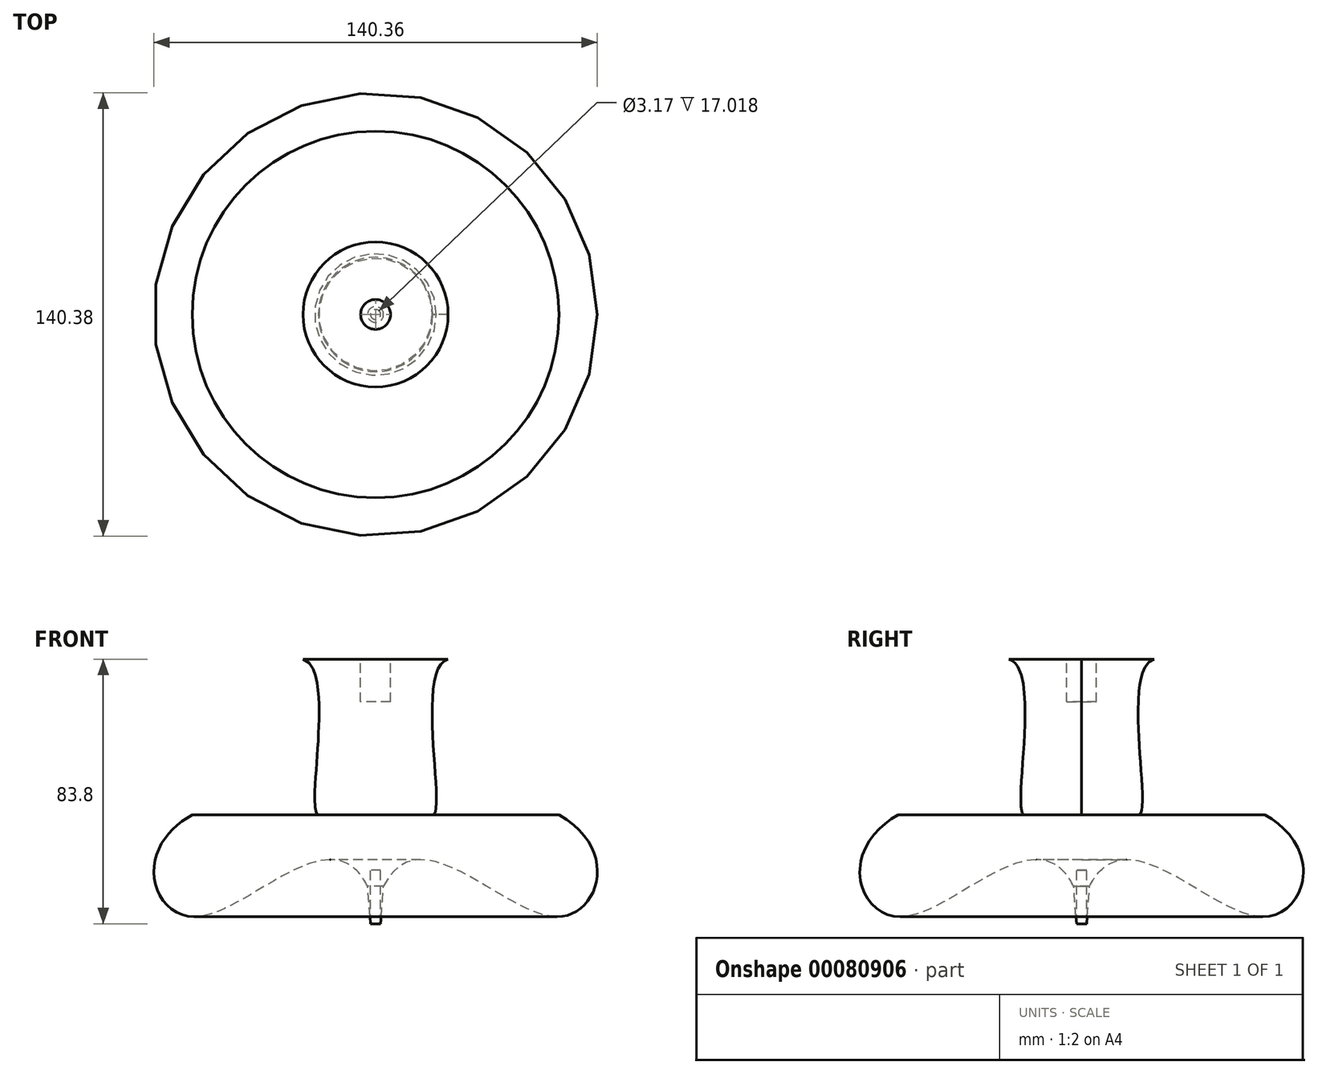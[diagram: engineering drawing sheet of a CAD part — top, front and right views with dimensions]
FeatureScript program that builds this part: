
annotation { "Feature Type Name" : "Feature", "Feature Type Description" : "" }
export const myFeature = defineFeature(function(context is Context, id is Id, definition is map)
    precondition{}
    {
        {
            var Q0;
            Q0=qCreatedBy(makeId("Front.planeOp"),FACE);
            var sketch = newSketch(context, id + "F0", { "sketchPlane" : qUnion([Q0])});
            skLineSegment(sketch, "E0", {"start": v(-18.1, 0) * mm, "end": v(-58.05, 0) * mm});
            skFitSpline(sketch, "E1", {"points": [v(-58.05, 0) * mm, v(-58.05, -32.28) * mm, v(-2.53, -22.64) * mm], "startDerivative": vector(-135.02, -76.93) * mm, "endDerivative": vector(62.62, -125.23) * mm});
            skLineSegment(sketch, "E2", {"start": v(-2.53, -22.64) * mm, "end": v(-1.59, -34.5) * mm});
            skLineSegment(sketch, "E3", {"start": v(0, 35.76) * mm, "end": v(0, -17.48) * mm});
            skFitSpline(sketch, "E4", {"points": [v(0, 49.3) * mm, v(-25.2, 49.3) * mm], "startDerivative": vector(-24.15, 0) * mm, "endDerivative": vector(-24.15, 0) * mm});
            skFitSpline(sketch, "E5", {"points": [v(-25.2, 49.3) * mm, v(-18.1, 0) * mm], "startDerivative": vector(42.7, 9.4) * mm, "endDerivative": vector(13.88, 0) * mm});
            skLineSegment(sketch, "E6", {"start": v(-22.96, 49.3) * mm, "end": v(-4.73, 49.3) * mm});
            skLineSegment(sketch, "E7", {"start": v(-4.73, 49.3) * mm, "end": v(-4.73, 35.76) * mm});
            skLineSegment(sketch, "E8", {"start": v(-4.73, 35.76) * mm, "end": v(0, 35.76) * mm});
            skLineSegment(sketch, "E9", {"start": v(-1.59, -34.5) * mm, "end": v(-1.59, -17.48) * mm});
            skLineSegment(sketch, "E10", {"start": v(-1.59, -17.48) * mm, "end": v(0, -17.48) * mm});
            skPoint(sketch, "E11.orphan", {"position": v(0, -54.57) * mm});
            skPoint(sketch, "E12.end.orphan", {"position": v(0, -52.28) * mm});
            skSolve(sketch);
        }
        {
            var Q0;
            Q0=makeQuery(id+"F0.imprint","IMPRINT",FACE,{"disambiguationData":[TD([[makeQuery(id+"F0.imprint","IMPRINT",EDGE,{"derivedFrom":sQuery(id+"F0.wireOp",EDGE,"E0")}),1.0]])]});
            var Q1;
            Q1=sQuery(id+"F0.wireOp",EDGE,"E6");
            var Q2;
            Q2=sQuery(id+"F0.wireOp",EDGE,"E7");
            var Q3;
            Q3=sQuery(id+"F0.wireOp",EDGE,"E5");
            var Q4;
            Q4=sQuery(id+"F0.wireOp",EDGE,"E8");
            var Q5;
            Q5=sQuery(id+"F0.wireOp",EDGE,"E0");
            var Q6;
            Q6=sQuery(id+"F0.wireOp",EDGE,"E1");
            var Q7;
            Q7=sQuery(id+"F0.wireOp",EDGE,"E2");
            var Q8;
            Q8=sQuery(id+"F0.wireOp",EDGE,"E9");
            var Q9;
            Q9=sQuery(id+"F0.wireOp",EDGE,"E10");
            var Q10;
            Q10=sQuery(id+"F0.wireOp",EDGE,"E3");
            revolve(context, id + "F1", {"entities" : qUnion([Q0]), "surfaceEntities" : qUnion([Q1, Q2, Q3, Q4, Q5, Q6, Q7, Q8, Q9]), "axis" : qUnion([Q10]), "revolveType" : RevolveType.FULL});
        }
    });
